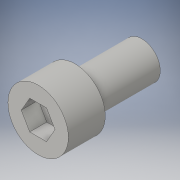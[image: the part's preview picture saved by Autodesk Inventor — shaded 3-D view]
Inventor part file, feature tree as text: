
AUTODESK INVENTOR PART (.ipt)
format: ipt  version: 2016 (Build 200138000, 138)  size: 124,416 bytes
history: native  units: in
note: dims shown in document units (in); Inventor stores cm internally (conversion verified against a paired STEP export)
features: other x13, extrude x3, sketch x3
ambient origin geometry x8: Origin, YZ Plane, XZ Plane, XY Plane, X Axis, Y Axis, Z Axis, Center Point
bodies: Solid1 (feature_tree)
feature tree (19):
  other  "Table"
  other  "shcs-6-0250"
  other  "shcs-6-0500"
  other  "shcs-6-0750"
  other  "shcs-6-1000"
  other  "shcs-6-1250"
  other  "shcs-6-1500"
  other  "shcs-6-1750"
  other  "shcs-6-2000"
  other  "shcs-6-2250"
  other  "shcs-6-2500"
  other  "shcs-6-2750"
  other  "shcs-6-3000"
  extrude  "Extrusion1"  TaperAngle=0.0deg  [1 undecoded]
  extrude  "Extrusion2"  [1 undecoded]
  extrude  "Extrusion3"  [1 undecoded]
  sketch  "Sketch1"  dims[d1=0.0in d4=0.0in]
  sketch  "Sketch2"  dims[d7=0.0in]
  sketch  "Sketch3"
note: 3 required parameter values undecoded (feature->parameter linkage not recoverable at this tier; creation-order binding heuristic only, values carry confidence <= 0.55)
